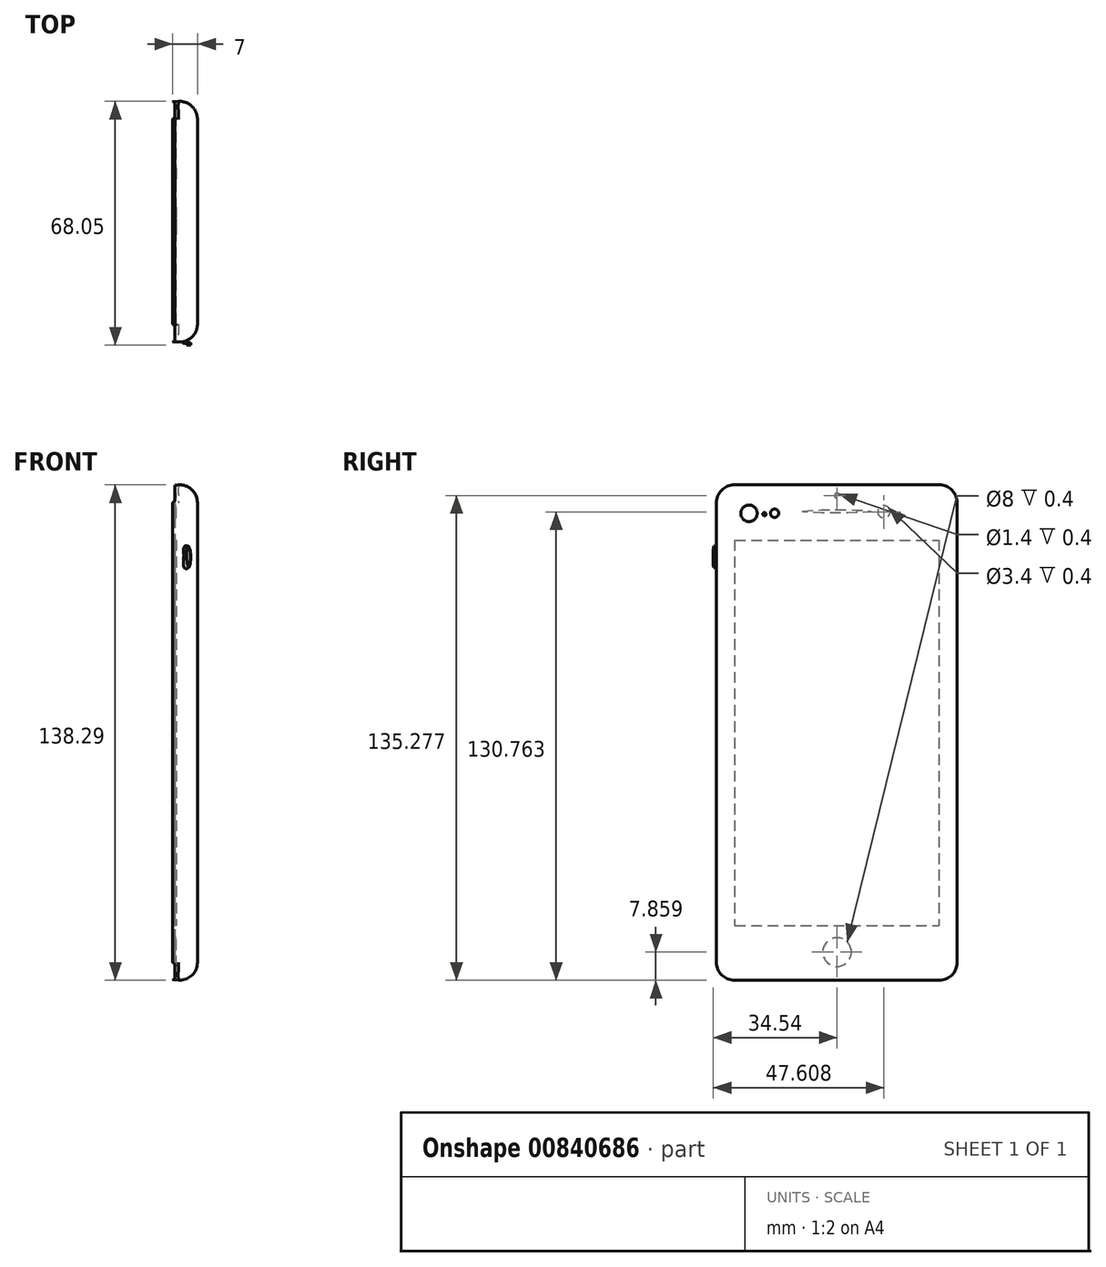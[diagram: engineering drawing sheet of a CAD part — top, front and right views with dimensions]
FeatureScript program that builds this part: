
annotation { "Feature Type Name" : "Feature", "Feature Type Description" : "" }
export const myFeature = defineFeature(function(context is Context, id is Id, definition is map)
    precondition{}
    {
        {
            var Q0;
            Q0=qCreatedBy(makeId("Right.planeOp"),FACE);
            var sketch = newSketch(context, id + "F0", { "sketchPlane" : qUnion([Q0])});
            skLineSegment(sketch, "E0.bottom", {"start": v(-33.58, 68.51) * mm, "end": v(33.42, 68.51) * mm});
            skLineSegment(sketch, "E0.top", {"start": v(-33.58, -69.59) * mm, "end": v(33.42, -69.59) * mm});
            skLineSegment(sketch, "E0.left", {"start": v(-33.58, 68.51) * mm, "end": v(-33.58, -69.59) * mm});
            skLineSegment(sketch, "E0.right", {"start": v(33.42, 68.51) * mm, "end": v(33.42, -69.59) * mm});
            skSolve(sketch);
        }
        {
            var Q0;
            Q0=makeQuery(id+"F0.imprint","IMPRINT",FACE,{"disambiguationData":[TD([[makeQuery(id+"F0.imprint","IMPRINT",EDGE,{"derivedFrom":sQuery(id+"F0.wireOp",EDGE,"E0.bottom")}),-1.0]])]});
            var sketch = newSketch(context, id + "F1", { "sketchPlane" : qUnion([Q0])});
            skLineSegment(sketch, "E1.bottom", {"start": v(-28.58, 53.18) * mm, "end": v(28.42, 53.18) * mm});
            skLineSegment(sketch, "E1.top", {"start": v(-28.58, -54.46) * mm, "end": v(28.42, -54.46) * mm});
            skLineSegment(sketch, "E1.left", {"start": v(-28.58, 53.18) * mm, "end": v(-28.58, -54.46) * mm});
            skLineSegment(sketch, "E1.right", {"start": v(28.42, 53.18) * mm, "end": v(28.42, -54.46) * mm});
            skSolve(sketch);
        }
        {
            var Q0;
            Q0=makeQuery(id+"F0.imprint","IMPRINT",FACE,{"disambiguationData":[TD([[makeQuery(id+"F0.imprint","IMPRINT",EDGE,{"derivedFrom":sQuery(id+"F0.wireOp",EDGE,"E0.bottom")}),-1.0]])]});
            var sketch = newSketch(context, id + "F2", { "sketchPlane" : qUnion([Q0])});
            skFitSpline(sketch, "E2", {"points": [v(-9.69, 61.2) * mm, v(0, 61.67) * mm, v(9.47, 61.24) * mm, v(0, 60.72) * mm, v(-9.69, 61.2) * mm]});
            skSolve(sketch);
        }
        {
            var Q0;
            Q0=makeQuery(id+"F0.imprint","IMPRINT",FACE,{"disambiguationData":[TD([[makeQuery(id+"F0.imprint","IMPRINT",EDGE,{"derivedFrom":sQuery(id+"F0.wireOp",EDGE,"E0.bottom")}),-1.0]])]});
            var sketch = newSketch(context, id + "F3", { "sketchPlane" : qUnion([Q0])});
            skCircle(sketch, "E3", {"center": v(13.07, 61.08) * mm, "radius": 1.7 * mm});
            skCircle(sketch, "E4", {"center": v(0, 65.6) * mm, "radius": 0.7 * mm});
            skSolve(sketch);
        }
        {
            var Q0;
            Q0=makeQuery(id+"F0.imprint","IMPRINT",FACE,{"disambiguationData":[TD([[makeQuery(id+"F0.imprint","IMPRINT",EDGE,{"derivedFrom":sQuery(id+"F0.wireOp",EDGE,"E0.bottom")}),-1.0]])]});
            var sketch = newSketch(context, id + "F4", { "sketchPlane" : qUnion([Q0])});
            skCircle(sketch, "E5", {"center": v(0, -61.82) * mm, "radius": 4 * mm});
            skSolve(sketch);
        }
        {
            var Q0;
            Q0=makeQuery(id+"F0.imprint","IMPRINT",FACE,{"disambiguationData":[TD([[makeQuery(id+"F0.imprint","IMPRINT",EDGE,{"derivedFrom":sQuery(id+"F0.wireOp",EDGE,"E0.bottom")}),-1.0]])]});
            extrude(context, id + "F5", {"entities" : qUnion([Q0]), "depth" : 6.9 * mm, "offsetDistance" : 25 * mm, "hasDraft" : true, "draftAngle" : 3 * degree});
        }
        {
            var Q0;
            Q0 = qSketchRegion(id + "F4", true);
            extrude(context, id + "F6", {"entities" : qUnion([Q0]), "operationType" : NewBodyOperationType.REMOVE, "depth" : 1 * mm, "offsetDistance" : 25 * mm});
        }
        {
            var Q0;
            Q0=makeQuery(id+"F1.imprint","IMPRINT",FACE,{"disambiguationData":[TD([[makeQuery(id+"F1.imprint","IMPRINT",EDGE,{"derivedFrom":sQuery(id+"F1.wireOp",EDGE,"E1.bottom")}),-1.0]])]});
            extrude(context, id + "F7", {"entities" : qUnion([Q0]), "operationType" : NewBodyOperationType.REMOVE, "depth" : 1 * mm, "offsetDistance" : 25 * mm});
        }
        {
            var Q0;
            Q0=makeQuery(id+"F2.imprint","IMPRINT",FACE,{"disambiguationData":[TD([[makeQuery(id+"F2.imprint","IMPRINT",EDGE,{"derivedFrom":sQuery(id+"F2.wireOp",EDGE,"E2")}),1.0]])]});
            extrude(context, id + "F8", {"entities" : qUnion([Q0]), "operationType" : NewBodyOperationType.REMOVE, "depth" : 0.6 * mm, "offsetDistance" : 25 * mm});
        }
        {
            var Q0;
            Q0 = qSketchRegion(id + "F3", true);
            extrude(context, id + "F9", {"entities" : qUnion([Q0]), "operationType" : NewBodyOperationType.REMOVE, "depth" : 1 * mm, "offsetDistance" : 25 * mm});
        }
        {
            var Q0;
            {var subQ0=sQuery(id+"F0.wireOp",EDGE,"E0.bottom");Q0=makeQuery(id+"F8.boolean.opBoolean","MERGE",EDGE,{"derivedFrom":[makeQuery(id+"F5.opExtrude","CAP_EDGE",EDGE,{"disambiguationData":[OSD([subQ0])],"isStart":true}),makeQuery(id+"F8.opExtrude","CAP_EDGE",EDGE,{"disambiguationData":[OSD([subQ0])],"isStart":true})]});}
            var Q1;
            Q1=makeQuery(id+"F5.opExtrude","CAP_EDGE",EDGE,{"disambiguationData":[OSD([sQuery(id+"F0.wireOp",EDGE,"E0.bottom")])],"isStart":false});
            var Q2;
            Q2=makeQuery(id+"F5.opExtrude","CAP_EDGE",EDGE,{"disambiguationData":[OSD([sQuery(id+"F0.wireOp",EDGE,"E0.right")])],"isStart":false});
            fillet(context, id + "F10", {"entities" : qUnion([Q0, Q1, Q2]), "radius" : 5 * mm, "tangentPropagation" : true, "allowEdgeOverflow" : false});
        }
        {
            var Q0;
            Q0=makeQuery(id+"F5.opExtrude","CAP_EDGE",EDGE,{"disambiguationData":[OSD([sQuery(id+"F0.wireOp",EDGE,"E0.left")])],"isStart":false});
            var Q1;
            Q1=makeQuery(id+"F5.opExtrude","SWEPT_EDGE",EDGE,{"disambiguationData":[OSD([sQuery(id+"F0.wireOp",EDGE,"E0.top"),sQuery(id+"F0.wireOp",EDGE,"E0.left")])]});
            fillet(context, id + "F11", {"entities" : qUnion([Q0, Q1]), "radius" : 5 * mm, "tangentPropagation" : true, "allowEdgeOverflow" : false});
        }
        {
            var Q0;
            Q0=makeQuery(id+"F10.opFillet","BLEND_EDGE",EDGE,{"blendedFrom":[makeQuery(id+"F5.opExtrude","CAP_EDGE",EDGE,{"disambiguationData":[OSD([sQuery(id+"F0.wireOp",EDGE,"E0.bottom")])],"isStart":false}),makeQuery(id+"F5.opExtrude","CAP_EDGE",EDGE,{"disambiguationData":[OSD([sQuery(id+"F0.wireOp",EDGE,"E0.right")])],"isStart":false})],"blendedInto":[]});
            fillet(context, id + "F12", {"entities" : qUnion([Q0]), "radius" : 5 * mm, "tangentPropagation" : true, "allowEdgeOverflow" : false});
        }
        {
            var Q0;
            Q0=makeQuery(id+"F5.opExtrude","CAP_EDGE",EDGE,{"disambiguationData":[OSD([sQuery(id+"F0.wireOp",EDGE,"E0.top")])],"isStart":false});
            fillet(context, id + "F13", {"entities" : qUnion([Q0]), "radius" : 5 * mm, "tangentPropagation" : true, "allowEdgeOverflow" : false});
        }
        {
            var Q0;
            Q0=makeQuery(id+"F5.opExtrude","SWEPT_FACE",FACE,{"disambiguationData":[OSD([sQuery(id+"F0.wireOp",EDGE,"E0.left")])]});
            var sketch = newSketch(context, id + "F14", { "sketchPlane" : qUnion([Q0])});
            skFitSpline(sketch, "E6", {"points": [v(5.67, 48.78) * mm, v(6.1, 51.53) * mm, v(6.77, 48.78) * mm, v(6.24, 45.57) * mm, v(5.67, 48.78) * mm]});
            skSolve(sketch);
        }
        {
            var Q0;
            {var subQ0=sQuery(id+"F0.wireOp",EDGE,"E0.left");Q0=makeQuery(id+"F14.imprint","IMPRINT",FACE,{"disambiguationData":[TD([[makeQuery(id+"F14.imprint","IMPRINT",EDGE,{"derivedFrom":makeQuery(id+"F8.boolean.opBoolean","MERGE",EDGE,{"derivedFrom":[makeQuery(id+"F5.opExtrude","CAP_EDGE",EDGE,{"disambiguationData":[OSD([subQ0])],"isStart":true}),makeQuery(id+"F8.opExtrude","CAP_EDGE",EDGE,{"disambiguationData":[OSD([subQ0])],"isStart":true})]})}),1.0]])]});}
            var sketch = newSketch(context, id + "F15", { "sketchPlane" : qUnion([Q0])});
            skFitSpline(sketch, "E7", {"points": [v(5.75, 51.55) * mm, v(5.07, 51.47) * mm, v(4.85, 48.6) * mm, v(5.07, 45.36) * mm, v(6.05, 45.44) * mm, v(5.75, 48.68) * mm, v(5.75, 51.55) * mm]});
            skSolve(sketch);
        }
        {
            var Q0;
            Q0=makeQuery(id+"F15.imprint","IMPRINT",FACE,{"disambiguationData":[TD([[makeQuery(id+"F15.imprint","IMPRINT",EDGE,{"derivedFrom":sQuery(id+"F15.wireOp",EDGE,"E7")}),1.0]])]});
            var Q1;
            Q1=sQuery(id+"F15.wireOp",EDGE,"E7");
            extrude(context, id + "F16", {"entities" : qUnion([Q0]), "surfaceEntities" : qUnion([Q1]), "depth" : 0.3 * mm, "offsetDistance" : 25 * mm});
        }
        {
            var Q0;
            Q0=makeQuery(id+"F14.imprint","IMPRINT",FACE,{"disambiguationData":[TD([[makeQuery(id+"F14.imprint","IMPRINT",EDGE,{"derivedFrom":sQuery(id+"F14.wireOp",EDGE,"E6")}),-1.0]])]});
            extrude(context, id + "F17", {"entities" : qUnion([Q0]), "operationType" : NewBodyOperationType.ADD, "depth" : 0.7 * mm, "offsetDistance" : 25 * mm});
        }
        {
            var Q0;
            Q0=makeQuery(id+"F5.opExtrude","CAP_FACE",FACE,{"disambiguationData":[OSD([sQuery(id+"F0.wireOp",EDGE,"E0.bottom"),sQuery(id+"F0.wireOp",EDGE,"E0.top"),sQuery(id+"F0.wireOp",EDGE,"E0.left"),sQuery(id+"F0.wireOp",EDGE,"E0.right")])],"isStart":false});
            var sketch = newSketch(context, id + "F18", { "sketchPlane" : qUnion([Q0])});
            skCircle(sketch, "E8", {"center": v(-24.59, 60.67) * mm, "radius": 2.3 * mm});
            skSolve(sketch);
        }
        {
            var Q0;
            Q0=makeQuery(id+"F18.imprint","IMPRINT",FACE,{"disambiguationData":[TD([[makeQuery(id+"F18.imprint","IMPRINT",EDGE,{"derivedFrom":sQuery(id+"F18.wireOp",EDGE,"E8")}),1.0]])]});
            var sketch = newSketch(context, id + "F19", { "sketchPlane" : qUnion([Q0])});
            skCircle(sketch, "E9", {"center": v(-24.54, 60.69) * mm, "radius": 1.85 * mm});
            skSolve(sketch);
        }
        {
            var Q0;
            Q0 = qSketchRegion(id + "F18", true);
            extrude(context, id + "F20", {"entities" : qUnion([Q0]), "depth" : 0.1 * mm, "offsetDistance" : 25 * mm});
        }
        {
            var Q0;
            Q0=sQuery(id+"F19.wireOp",EDGE,"E9");
            extrude(context, id + "F21", {"bodyType" : ToolBodyType.SURFACE, "surfaceEntities" : qUnion([Q0]), "depth" : 0.2 * mm, "offsetDistance" : 25 * mm});
        }
        {
            var Q0;
            Q0=makeQuery(id+"F5.opExtrude","CAP_FACE",FACE,{"disambiguationData":[OSD([sQuery(id+"F0.wireOp",EDGE,"E0.bottom"),sQuery(id+"F0.wireOp",EDGE,"E0.top"),sQuery(id+"F0.wireOp",EDGE,"E0.left"),sQuery(id+"F0.wireOp",EDGE,"E0.right")])],"isStart":false});
            var sketch = newSketch(context, id + "F22", { "sketchPlane" : qUnion([Q0])});
            skCircle(sketch, "E10", {"center": v(-20.28, 60.43) * mm, "radius": 0.46 * mm});
            skSolve(sketch);
        }
        {
            var Q0;
            Q0 = qSketchRegion(id + "F22", true);
            extrude(context, id + "F23", {"entities" : qUnion([Q0]), "depth" : 0.1 * mm, "offsetDistance" : 25 * mm});
        }
        {
            var Q0;
            Q0=makeQuery(id+"F5.opExtrude","CAP_FACE",FACE,{"disambiguationData":[OSD([sQuery(id+"F0.wireOp",EDGE,"E0.bottom"),sQuery(id+"F0.wireOp",EDGE,"E0.top"),sQuery(id+"F0.wireOp",EDGE,"E0.left"),sQuery(id+"F0.wireOp",EDGE,"E0.right")])],"isStart":false});
            var sketch = newSketch(context, id + "F24", { "sketchPlane" : qUnion([Q0])});
            skCircle(sketch, "E11", {"center": v(-17.45, 60.7) * mm, "radius": 1.16 * mm});
            skSolve(sketch);
        }
        {
            var Q0;
            Q0 = qSketchRegion(id + "F24", true);
            extrude(context, id + "F25", {"entities" : qUnion([Q0]), "depth" : 0.1 * mm, "offsetDistance" : 25 * mm});
        }
    });
